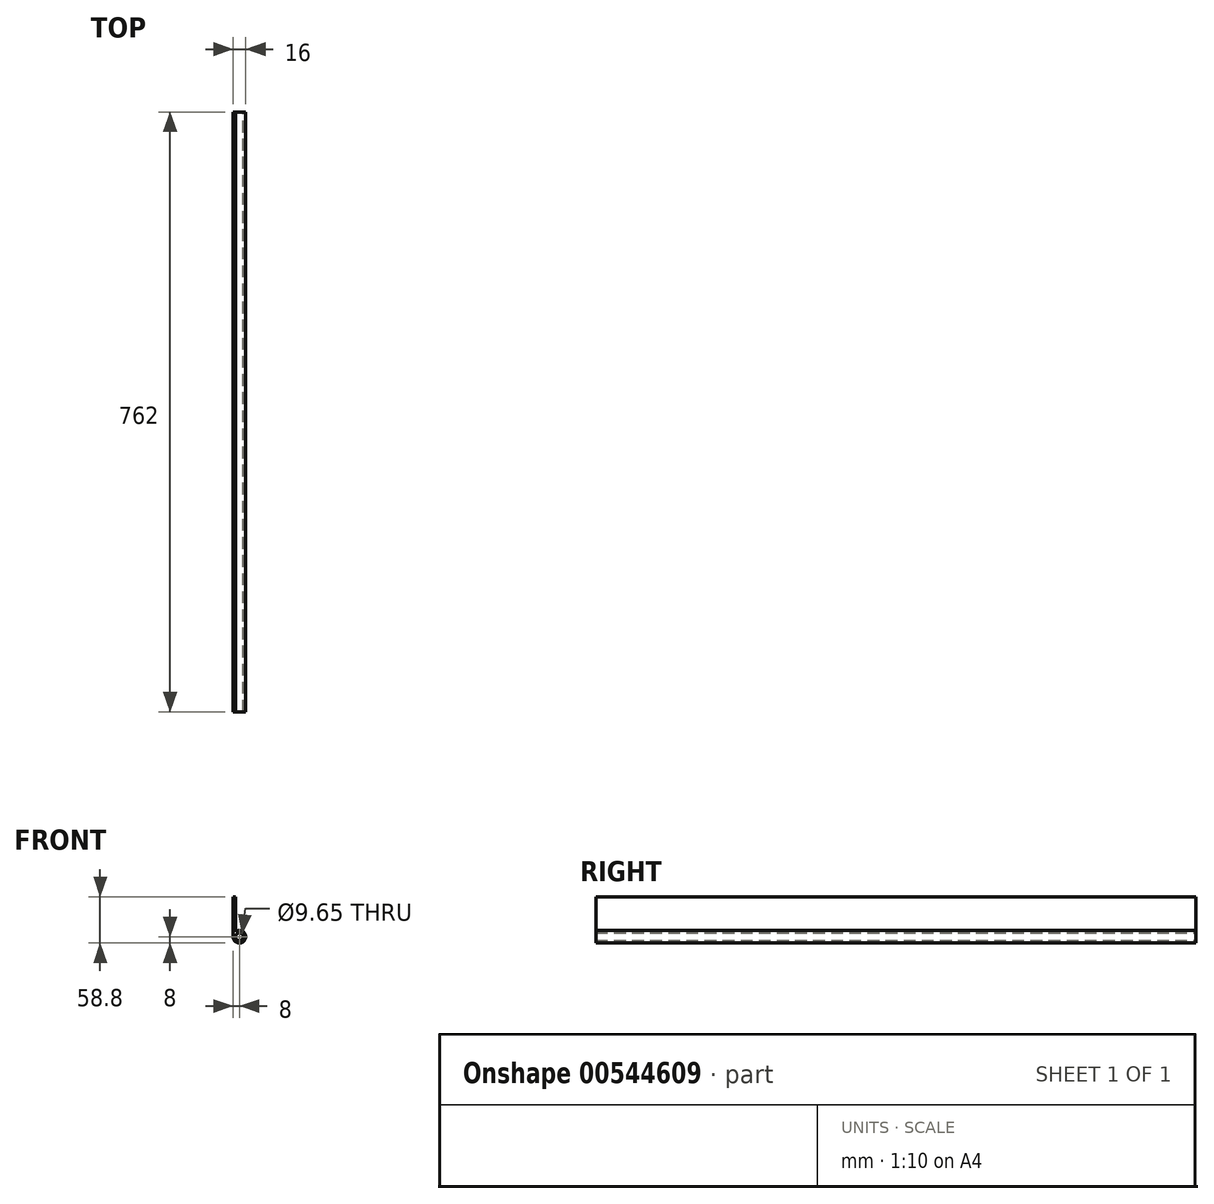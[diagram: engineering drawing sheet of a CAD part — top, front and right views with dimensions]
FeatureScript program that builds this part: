
annotation { "Feature Type Name" : "Feature", "Feature Type Description" : "" }
export const myFeature = defineFeature(function(context is Context, id is Id, definition is map)
    precondition{}
    {
        {
            var Q0;
            Q0=qCreatedBy(makeId("Front.planeOp"),FACE);
            var sketch = newSketch(context, id + "F0", { "sketchPlane" : qUnion([Q0])});
            skCircle(sketch, "E0", {"center": v(0, 0) * mm, "radius": 4.83 * mm});
            skArc(sketch, "E1.0", {"start": v(-8, 0) * mm, "mid": v(0, -8) * mm, "end": v(8, 0) * mm});
            skLineSegment(sketch, "E2", {"start": v(-8, 0) * mm, "end": v(-8, 50.8) * mm});
            skLineSegment(sketch, "E3.0", {"start": v(-4.83, 6.38) * mm, "end": v(-4.83, 50.8) * mm});
            skLineSegment(sketch, "E4", {"start": v(-8, 50.8) * mm, "end": v(-4.83, 50.8) * mm});
            skArc(sketch, "E5.trimOffspring", {"start": v(8, 0) * mm, "mid": v(3.56, 7.16) * mm, "end": v(-4.83, 6.38) * mm});
            skSolve(sketch);
        }
        {
            var Q0;
            Q0 = qSketchRegion(id + "F0", true);
            extrude(context, id + "F1", {"entities" : qUnion([Q0]), "endBound" : BoundingType.SYMMETRIC, "depth" : 762 * mm, "offsetDistance" : 25.4 * mm});
        }
    });
